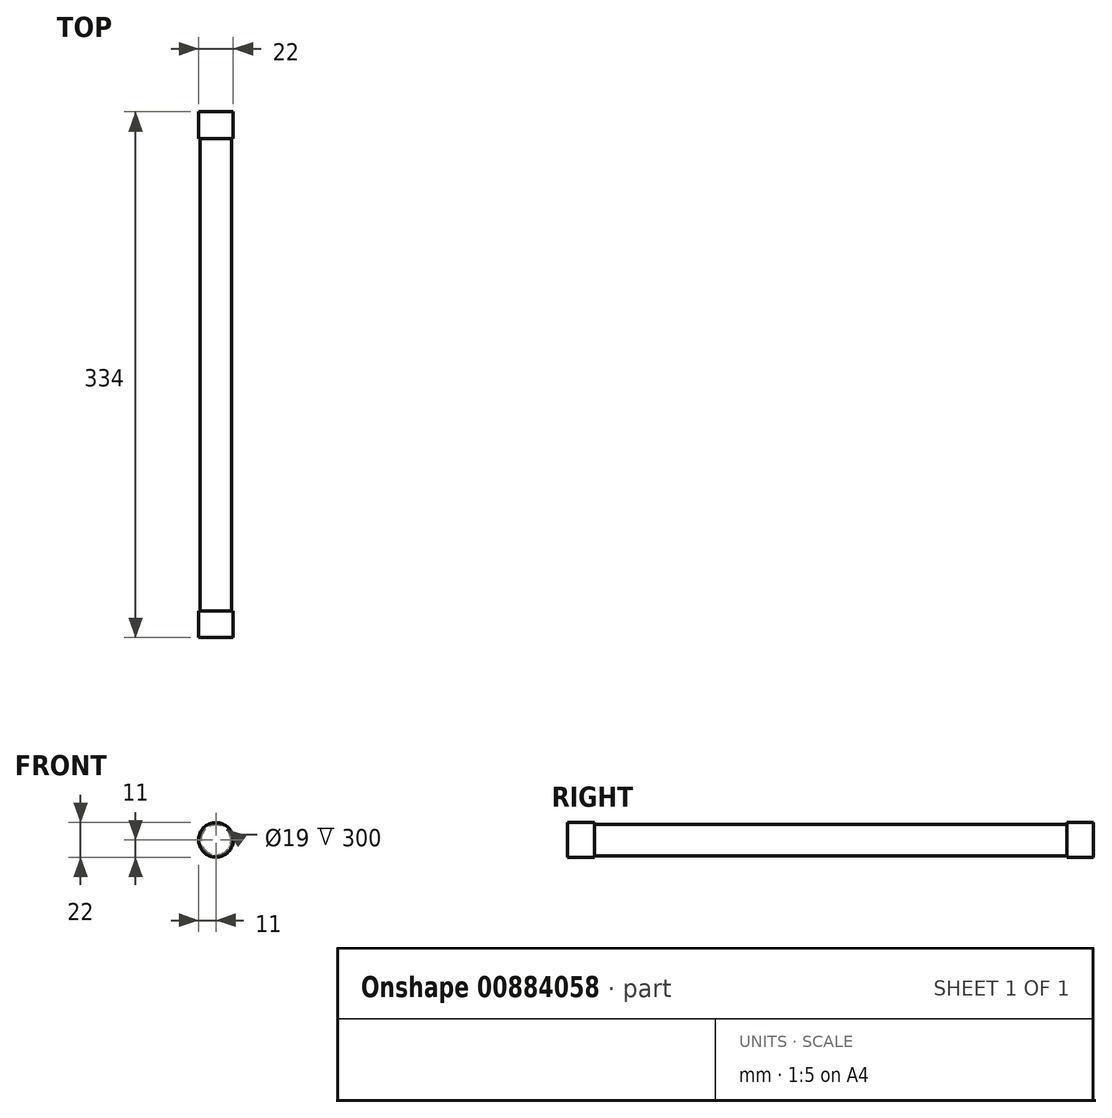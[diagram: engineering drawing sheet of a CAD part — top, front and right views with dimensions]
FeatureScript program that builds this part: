
annotation { "Feature Type Name" : "Feature", "Feature Type Description" : "" }
export const myFeature = defineFeature(function(context is Context, id is Id, definition is map)
    precondition{}
    {
        {
            var Q0;
            Q0=qCreatedBy(makeId("Front.planeOp"),FACE);
            var sketch = newSketch(context, id + "F0", { "sketchPlane" : qUnion([Q0])});
            skCircle(sketch, "E0", {"center": v(0, 0) * mm, "radius": 10 * mm});
            skCircle(sketch, "E1", {"center": v(0, 0) * mm, "radius": 9.5 * mm});
            skSolve(sketch);
        }
        {
            var Q0;
            Q0 = qSketchRegion(id + "F0", true);
            extrude(context, id + "F1", {"entities" : qUnion([Q0]), "depth" : 300 * mm, "offsetDistance" : 25 * mm});
        }
        {
            var Q0;
            Q0=qCreatedBy(makeId("Top.planeOp"),FACE);
            var sketch = newSketch(context, id + "F2", { "sketchPlane" : qUnion([Q0])});
            skLineSegment(sketch, "E2", {"start": v(0, -558.76) * mm, "end": v(0, -471.8) * mm, "construction": true});
            skLineSegment(sketch, "E3", {"start": v(0, -300) * mm, "end": v(11, -300) * mm});
            skLineSegment(sketch, "E4", {"start": v(11, -300) * mm, "end": v(11, -317) * mm});
            skLineSegment(sketch, "E5", {"start": v(11, -317) * mm, "end": v(1.93, -317) * mm});
            skLineSegment(sketch, "E6", {"start": v(1.93, -317) * mm, "end": v(0, -317) * mm});
            skLineSegment(sketch, "E7", {"start": v(0, -317) * mm, "end": v(0, -300) * mm});
            skPoint(sketch, "E8.visualSharp", {"position": v(1.93, -317) * mm});
            skSolve(sketch);
        }
        {
            var Q0;
            Q0 = qSketchRegion(id + "F2", true);
            var Q1;
            Q1=sQuery(id+"F2.wireOp",EDGE,"E2");
            revolve(context, id + "F3", {"surfaceOperationType" : NewSurfaceOperationType.NEW, "entities" : qUnion([Q0]), "axis" : qUnion([Q1]), "revolveType" : RevolveType.FULL});
        }
        {
            var Q0;
            Q0=makeQuery(id+"F1.opExtrude","CAP_FACE",FACE,{"disambiguationData":[OSD([sQuery(id+"F0.wireOp",EDGE,"E0"),sQuery(id+"F0.wireOp",EDGE,"E1")])],"isStart":true});
            cPlane(context, id + "F4", {"entities" : qUnion([Q0]), "cplaneType" : CPlaneType.OFFSET, "offset" : 150 * mm, "oppositeDirection" : true, "width" : 150 * mm, "height" : 150 * mm});
        }
        {
            var Q0;
            Q0=makeQuery(id+"F3.opRevolve","SWEPT_BODY",BODY,{"disambiguationData":[OSD([sQuery(id+"F2.wireOp",EDGE,"E3"),sQuery(id+"F2.wireOp",EDGE,"E4"),sQuery(id+"F2.wireOp",EDGE,"E5"),sQuery(id+"F2.wireOp",EDGE,"E6"),sQuery(id+"F2.wireOp",EDGE,"E7")])]});
            var Q1;
            Q1=qCreatedBy(id+"F4.planeOp",FACE);
            mirror(context, id + "F5", {"operationType" : NewBodyOperationType.ADD, "entities" : qUnion([Q0]), "mirrorPlane" : qUnion([Q1])});
        }
    });
